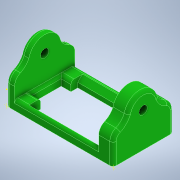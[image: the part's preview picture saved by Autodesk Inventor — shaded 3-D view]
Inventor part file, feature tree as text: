
AUTODESK INVENTOR PART (.ipt)
format: ipt  version: 2022 (Build 260153000, 153)  size: 241,152 bytes
history: native  units: in
note: dims shown in document units (in); Inventor stores cm internally (conversion verified against a paired STEP export)
features: sketch x5, extrude x3, fillet x2, chamfer x1
ambient origin geometry x8: Origin, YZ Plane, XZ Plane, XY Plane, X Axis, Y Axis, Z Axis, Center Point
bodies: Solid1 (feature_tree)
feature tree (11):
  extrude  "Extrusion1"  Depth=2.6378in TaperAngle=0.0deg
  extrude  "Extrusion2"  Depth=2.6378in TaperAngle=0.0deg
  sketch  "Sketch3"  dims[d12=0.1181in d13=0.0787in d14=45.0deg d15=0.0787in]
  fillet  "Fillet1"  Radius=0.0787in
  extrude  "Extrusion3"  Depth=0.1969in
  chamfer  "Chamfer1"  [1 undecoded]
  fillet  "Fillet2"  [1 undecoded]
  sketch  "Sketch5"
  sketch  "Sketch1"  dims[d5=2.6378in d6=0.0in d7=2.6378in d8=0.0in]
  sketch  "Sketch2"  dims[d9=0.2362in d10=2.6378in d11=0.0in]
  sketch  "Sketch4"  dims[d17=2.0866in d18=0.1969in]
note: 2 required parameter values undecoded (feature->parameter linkage not recoverable at this tier; creation-order binding heuristic only, values carry confidence <= 0.55)
